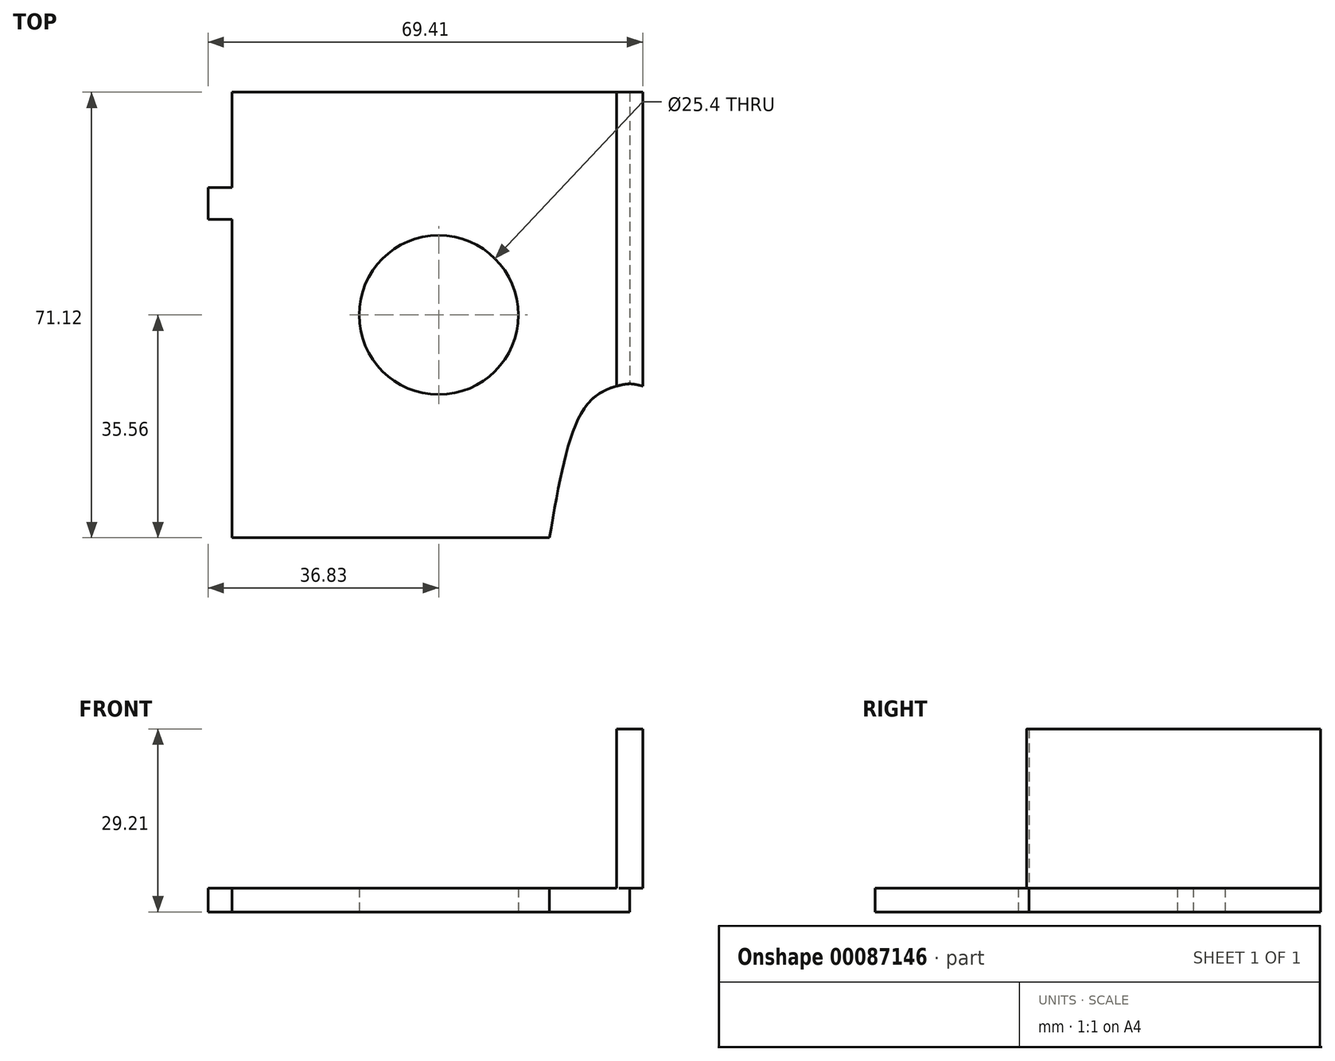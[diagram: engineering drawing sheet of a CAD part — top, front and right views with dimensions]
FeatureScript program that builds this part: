
annotation { "Feature Type Name" : "Feature", "Feature Type Description" : "" }
export const myFeature = defineFeature(function(context is Context, id is Id, definition is map)
    precondition{}
    {
        {
            var Q0;
            Q0=qCreatedBy(makeId("Top.planeOp"),FACE);
            var sketch = newSketch(context, id + "F0", { "sketchPlane" : qUnion([Q0])});
            skLineSegment(sketch, "E0.top", {"start": v(-63.5, 35.56) * mm, "end": v(63.5, 35.56) * mm});
            skLineSegment(sketch, "E0.left", {"start": v(-63.5, -35.56) * mm, "end": v(-63.5, 15.24) * mm});
            skLineSegment(sketch, "E0.right", {"start": v(63.5, -35.56) * mm, "end": v(63.5, 15.24) * mm});
            skPoint(sketch, "E0.middle", {"position": v(0, 0) * mm});
            skLineSegment(sketch, "E1", {"start": v(63.5, 0) * mm, "end": v(30.48, 0) * mm});
            skPoint(sketch, "E1.endSnap0", {"position": v(63.5, 0) * mm});
            skCircle(sketch, "E2", {"center": v(30.48, 0) * mm, "radius": 12.7 * mm});
            skCircle(sketch, "E3.MirrorC", {"center": v(-30.48, 0) * mm, "radius": 12.7 * mm});
            skFitSpline(sketch, "E4", {"points": [v(12.78, -35.56) * mm, v(9.04, -18.62) * mm, v(4.6, -12.4) * mm, v(0, -11) * mm], "startDerivative": vector(-7.2, 42.95) * mm, "endDerivative": vector(-9.26, 0) * mm});
            skFitSpline(sketch, "E5.MirrorCS", {"points": [v(-12.78, -35.56) * mm, v(-9.04, -18.62) * mm, v(-4.6, -12.4) * mm, v(0, -11) * mm], "startDerivative": vector(7.2, 42.95) * mm, "endDerivative": vector(9.26, 0) * mm});
            skLineSegment(sketch, "E6", {"start": v(-63.5, -35.56) * mm, "end": v(-12.78, -35.56) * mm});
            skLineSegment(sketch, "E7", {"start": v(12.78, -35.56) * mm, "end": v(63.5, -35.56) * mm});
            skPoint(sketch, "E8.middle", {"position": v(-63.5, 0) * mm});
            skLineSegment(sketch, "E9", {"start": v(-63.5, 0) * mm, "end": v(-63.5, 15.24) * mm});
            skLineSegment(sketch, "E10.bottom", {"start": v(-63.5, 15.24) * mm, "end": v(-67.3, 15.24) * mm});
            skLineSegment(sketch, "E10.top", {"start": v(-63.5, 20.32) * mm, "end": v(-67.3, 20.32) * mm});
            skLineSegment(sketch, "E10.right", {"start": v(-67.3, 15.24) * mm, "end": v(-67.3, 20.32) * mm});
            skPoint(sketch, "E10.middle", {"position": v(-63.5, 17.78) * mm});
            skPoint(sketch, "E11.orphan", {"position": v(-59.69, 20.32) * mm});
            skPoint(sketch, "E12.orphan", {"position": v(-59.69, 15.24) * mm});
            skLineSegment(sketch, "E13.trimOffspring", {"start": v(-63.5, 20.32) * mm, "end": v(-63.5, 35.56) * mm});
            skLineSegment(sketch, "E14", {"start": v(0, 35.56) * mm, "end": v(0, -11) * mm});
            skLineSegment(sketch, "E15.MirrorCS", {"start": v(63.5, 20.32) * mm, "end": v(67.3, 20.32) * mm});
            skLineSegment(sketch, "E16.MirrorCS", {"start": v(67.3, 15.24) * mm, "end": v(67.3, 20.32) * mm});
            skLineSegment(sketch, "E17.MirrorCS", {"start": v(63.5, 15.24) * mm, "end": v(67.3, 15.24) * mm});
            skLineSegment(sketch, "E18.trimOffspring", {"start": v(63.5, 20.32) * mm, "end": v(63.5, 35.56) * mm});
            skSolve(sketch);
        }
        {
            var Q0;
            {var subQ1=sQuery(id+"F0.wireOp",EDGE,"E0.top");Q0=makeQuery(id+"F0.imprint","IMPRINT",FACE,{"disambiguationData":[TD([[makeQuery(id+"F0.imprint","IMPRINT",EDGE,{"derivedFrom":subQ1}),-1.0]])]});}
            extrude(context, id + "F1", {"entities" : qUnion([Q0]), "depth" : 3.8 * mm});
        }
        {
            var Q0;
            Q0=makeQuery(id+"F1.opExtrude","CAP_FACE",FACE,{"disambiguationData":[OSD([sQuery(id+"F0.wireOp",EDGE,"E0.top"),sQuery(id+"F0.wireOp",EDGE,"E0.left"),sQuery(id+"F0.wireOp",EDGE,"E0.right"),sQuery(id+"F0.wireOp",EDGE,"E2"),sQuery(id+"F0.wireOp",EDGE,"E3.MirrorC"),sQuery(id+"F0.wireOp",EDGE,"E4"),sQuery(id+"F0.wireOp",EDGE,"E5.MirrorCS"),sQuery(id+"F0.wireOp",EDGE,"E6"),sQuery(id+"F0.wireOp",EDGE,"E7")])],"isStart":false});
            var sketch = newSketch(context, id + "F2", { "sketchPlane" : qUnion([Q0])});
            skLineSegment(sketch, "E19", {"start": v(-2.1, -11.37) * mm, "end": v(-2.1, 35.56) * mm});
            skLineSegment(sketch, "E20.MirrorCS", {"start": v(2.1, -11.36) * mm, "end": v(2.1, 35.56) * mm});
            skLineSegment(sketch, "E21", {"start": v(-2.1, 35.56) * mm, "end": v(2.1, 35.56) * mm});
            skFitSpline(sketch, "E22", {"points": [v(-2.1, -11.37) * mm, v(0, -11) * mm, v(2.1, -11.36) * mm], "startDerivative": vector(4.2, 1.12) * mm, "endDerivative": vector(4.2, -1.11) * mm});
            skSolve(sketch);
        }
        {
            var Q0;
            Q0=qSketchRegion(id+"F2",true);
            extrude(context, id + "F3", {"entities" : qUnion([Q0]), "operationType" : NewBodyOperationType.ADD, "depth" : 25.4 * mm});
        }
    });
